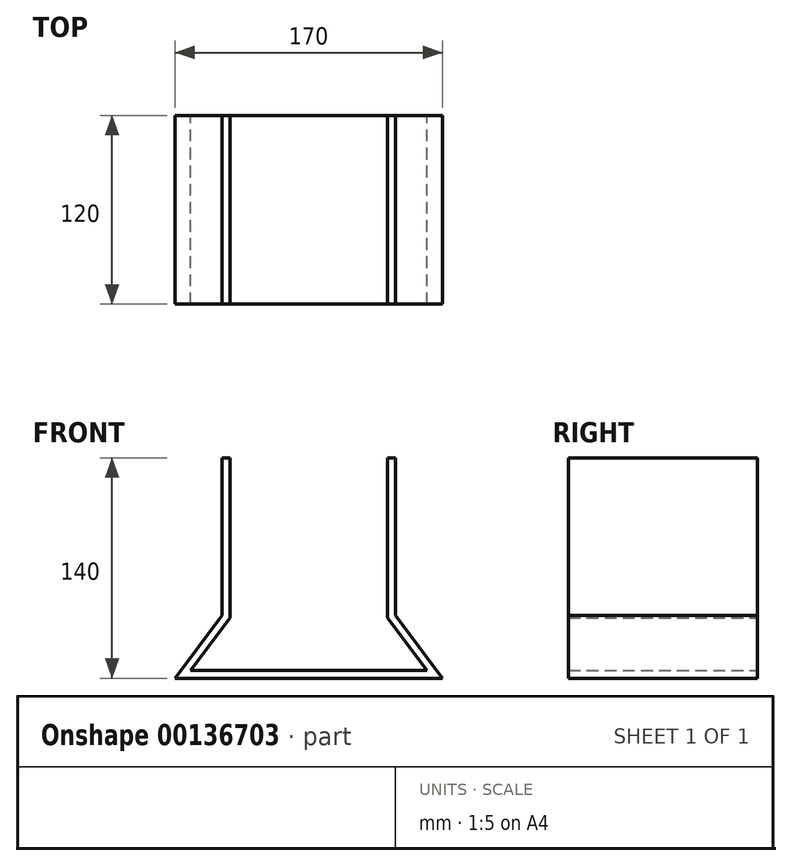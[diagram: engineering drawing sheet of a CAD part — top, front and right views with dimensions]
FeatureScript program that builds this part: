
annotation { "Feature Type Name" : "Feature", "Feature Type Description" : "" }
export const myFeature = defineFeature(function(context is Context, id is Id, definition is map)
    precondition{}
    {
        {
            var Q0;
            Q0=qCreatedBy(makeId("Front.planeOp"),FACE);
            var sketch = newSketch(context, id + "F0", { "sketchPlane" : qUnion([Q0])});
            skLineSegment(sketch, "E0.left", {"start": v(50, -50) * mm, "end": v(50, 50) * mm});
            skLineSegment(sketch, "E0.right", {"start": v(-50, -50) * mm, "end": v(-50, 50) * mm});
            skPoint(sketch, "E0.middle", {"position": v(0, 0) * mm});
            skLineSegment(sketch, "E1.bottom", {"start": v(-50, 50) * mm, "end": v(-55, 50) * mm});
            skLineSegment(sketch, "E1.left", {"start": v(-50, 50) * mm, "end": v(-50, -51.67) * mm});
            skLineSegment(sketch, "E1.right", {"start": v(-55, 50) * mm, "end": v(-55, -50) * mm});
            skLineSegment(sketch, "E2.bottom", {"start": v(50, 50) * mm, "end": v(55, 50) * mm});
            skLineSegment(sketch, "E2.left", {"start": v(50, 50) * mm, "end": v(50, -51.67) * mm});
            skLineSegment(sketch, "E2.right", {"start": v(55, 50) * mm, "end": v(55, -50) * mm});
            skLineSegment(sketch, "E3", {"start": v(85, -90) * mm, "end": v(-85, -90) * mm});
            skLineSegment(sketch, "E4", {"start": v(-85, -90) * mm, "end": v(-55, -50) * mm});
            skLineSegment(sketch, "E5.MirrorCS", {"start": v(85, -90) * mm, "end": v(55, -50) * mm});
            skPoint(sketch, "E6.orphan", {"position": v(-55, -90) * mm});
            skPoint(sketch, "E7.orphan", {"position": v(55, -90) * mm});
            skLineSegment(sketch, "E8.0", {"start": v(75, -85) * mm, "end": v(-75, -85) * mm});
            skLineSegment(sketch, "E9.0", {"start": v(-75, -85) * mm, "end": v(-50, -51.67) * mm});
            skLineSegment(sketch, "E10.0", {"start": v(75, -85) * mm, "end": v(50, -51.67) * mm});
            skSolve(sketch);
        }
        {
            var Q0;
            {var subQ0=sQuery(id+"F0.wireOp",EDGE,"E1.bottom");Q0=makeQuery(id+"F0.imprint","IMPRINT",FACE,{"disambiguationData":[TD([[makeQuery(id+"F0.imprint","IMPRINT",EDGE,{"derivedFrom":subQ0}),1.0]])]});}
            extrude(context, id + "F1", {"entities" : qUnion([Q0]), "depth" : 120 * mm});
        }
    });
